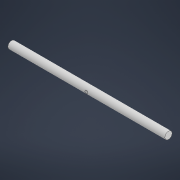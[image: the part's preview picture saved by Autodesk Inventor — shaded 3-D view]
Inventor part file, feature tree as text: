
AUTODESK INVENTOR PART (.ipt)
format: ipt  version: 2022 (Build 260153000, 153)  size: 104,960 bytes
history: native  units: in
note: dims shown in document units (in); Inventor stores cm internally (conversion verified against a paired STEP export)
features: extrude x1, fillet x1, sketch x1
ambient origin geometry x8: Origin, YZ Plane, XZ Plane, XY Plane, X Axis, Y Axis, Z Axis, Center Point
bodies: Solid1 (feature_tree)
feature tree (3):
  extrude  "Extrusion1"  Depth=0.5in
  fillet  "Fillet1"  Radius=0.3937in
  sketch  "Sketch1"  dims[d0=21.6535in d1=1.0in d2=0.3937in d3=1.0in d4=0.0in d5=0.5in d6=0.0in d7=0.0in d8=0.0in d9=0.0in]
